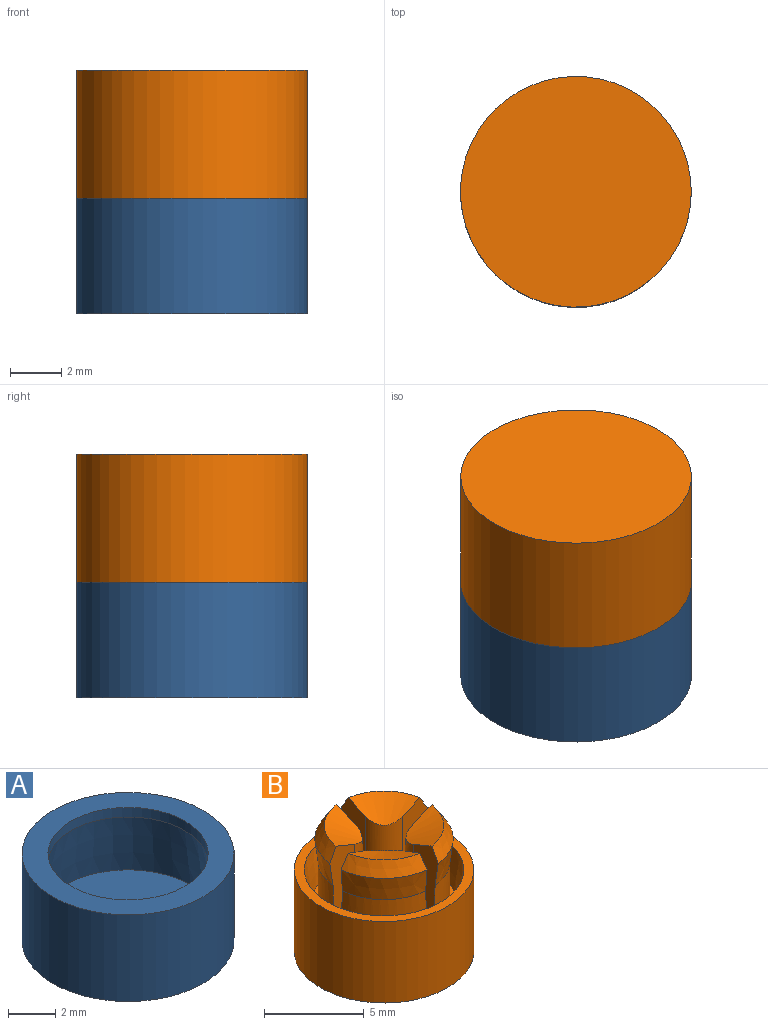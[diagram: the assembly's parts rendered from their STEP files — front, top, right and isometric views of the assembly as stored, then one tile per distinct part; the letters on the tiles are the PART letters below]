
ASSEMBLY  parts=2 mates=1
PART A: 6 faces, bbox 9x9x4.5 mm
  f0: plane 9x9mm, normal (0,0,1), area 27.3mm2, adj f2,f4
  f1: plane 7.52x7.52mm, normal (0,0,1), area 44.4mm2, adj f3
  f2: cylinder r=3.4mm len=6.8mm, axis (0,0,1), area 10.7mm2, adj f0,f3
  f3: cone r=3.4mm half-angle=6.8deg, axis (0,0,-1), area 68mm2, adj f1,f2
  f4: cylinder r=4.5mm len=9mm, axis (0,0,-1), area 127.2mm2, adj f0,f5
  f5: plane 9x9mm, normal (0,0,-1), area 63.6mm2, adj f4
PART B: 33 faces, bbox 9.1x9.1x7.8 mm
  f0: cylinder r=3.3mm len=3.07mm, axis (0,0,1), area 11.6mm2, adj f9,f14,f19,f20
  f1: cylinder r=3.3mm len=3.07mm, axis (0,0,1), area 11.6mm2, adj f10,f14,f23,f24
  f2: cylinder r=3.3mm len=3.07mm, axis (0,0,1), area 11.6mm2, adj f11,f14,f25,f26
  f3: cone r=0mm half-angle=67.9deg, axis (0,0,1), area 4.7mm2, adj f6,f19,f20,f27
  f4: cone r=0mm half-angle=67.9deg, axis (0,0,1), area 4.7mm2, adj f7,f23,f24,f30
  f5: cone r=0mm half-angle=67.9deg, axis (0,0,1), area 4.7mm2, adj f8,f25,f26,f28
  f6: cone r=3mm half-angle=30.4deg, axis (0,0,-1), area 3.9mm2, adj f3,f9,f19,f20
  f7: cone r=3mm half-angle=30.4deg, axis (0,0,-1), area 3.9mm2, adj f4,f10,f23,f24
  f8: cone r=3mm half-angle=30.4deg, axis (0,0,-1), area 3.9mm2, adj f5,f11,f25,f26
  f9: cone r=3.47mm half-angle=6.8deg, axis (0,0,1), area 6.5mm2, adj f0,f6,f19,f20
  f10: cone r=3.47mm half-angle=6.8deg, axis (0,0,1), area 6.5mm2, adj f1,f7,f23,f24
  f11: cone r=3.47mm half-angle=6.8deg, axis (0,0,1), area 6.5mm2, adj f2,f8,f25,f26
  f12: plane 9x9mm, normal (0,0,1), area 13.4mm2, adj f13,f32
  f13: cone r=4mm half-angle=10deg, axis (0,0,1), area 48.8mm2, adj f12,f14
  f14: plane 7.34x7.34mm, normal (0,0,1), area 14.8mm2, adj f0,f1,f2,f13,f15,f19,f20,f21
  f15: cylinder r=3.3mm len=3.07mm, axis (0,0,1), area 11.6mm2, adj f14,f18,f21,f22
  f16: cone r=0mm half-angle=67.9deg, axis (0,0,1), area 4.7mm2, adj f17,f21,f22,f29
  f17: cone r=3mm half-angle=30.4deg, axis (0,0,-1), area 3.9mm2, adj f16,f18,f21,f22
  f18: cone r=3.47mm half-angle=6.8deg, axis (0,0,1), area 6.5mm2, adj f15,f17,f21,f22
  f19: plane 4.77x1.98mm, normal (1,0,0.04), area 7.6mm2, adj f0,f3,f6,f9,f14,f27
  f20: plane 4.77x1.98mm, normal (0,-1,0.04), area 7.6mm2, adj f0,f3,f6,f9,f14,f27
  f21: plane 4.77x1.98mm, normal (0,1,0.04), area 7.6mm2, adj f14,f15,f16,f17,f18,f29
  f22: plane 4.77x1.98mm, normal (1,0,0.04), area 7.6mm2, adj f14,f15,f16,f17,f18,f29
  f23: plane 4.77x1.98mm, normal (-1,0,0.04), area 7.6mm2, adj f1,f4,f7,f10,f14,f30
  f24: plane 4.77x1.98mm, normal (0,1,0.04), area 7.6mm2, adj f1,f4,f7,f10,f14,f30
  f25: plane 4.77x1.98mm, normal (0,-1,0.04), area 7.6mm2, adj f2,f5,f8,f11,f14,f28
  f26: plane 4.77x1.98mm, normal (-1,0,0.04), area 7.6mm2, adj f2,f5,f8,f11,f14,f28
  f27: cylinder r=1.3mm len=4.24mm, axis (-0.04,0.04,1), area 8.6mm2, adj f3,f14,f19,f20
  f28: cylinder r=1.3mm len=4.24mm, axis (0.04,0.04,1), area 8.6mm2, adj f5,f14,f25,f26
  f29: cylinder r=1.3mm len=4.24mm, axis (-0.04,-0.04,1), area 8.6mm2, adj f14,f16,f21,f22
  f30: cylinder r=1.3mm len=4.24mm, axis (0.04,-0.04,1), area 8.6mm2, adj f4,f14,f23,f24
  f31: plane 9x9mm, normal (0,0,-1), area 63.6mm2, adj f32
  f32: cylinder r=4.5mm len=9mm, axis (0,0,-1), area 141.4mm2, adj f12,f31
PLACE A at identity
PLACE B rot(axis=(1,0,0),180deg) t=(0,0,0)mm
MATE planar B.f32 <-> A.f4  axis (0,0,-1) through (0,0,0)mm
